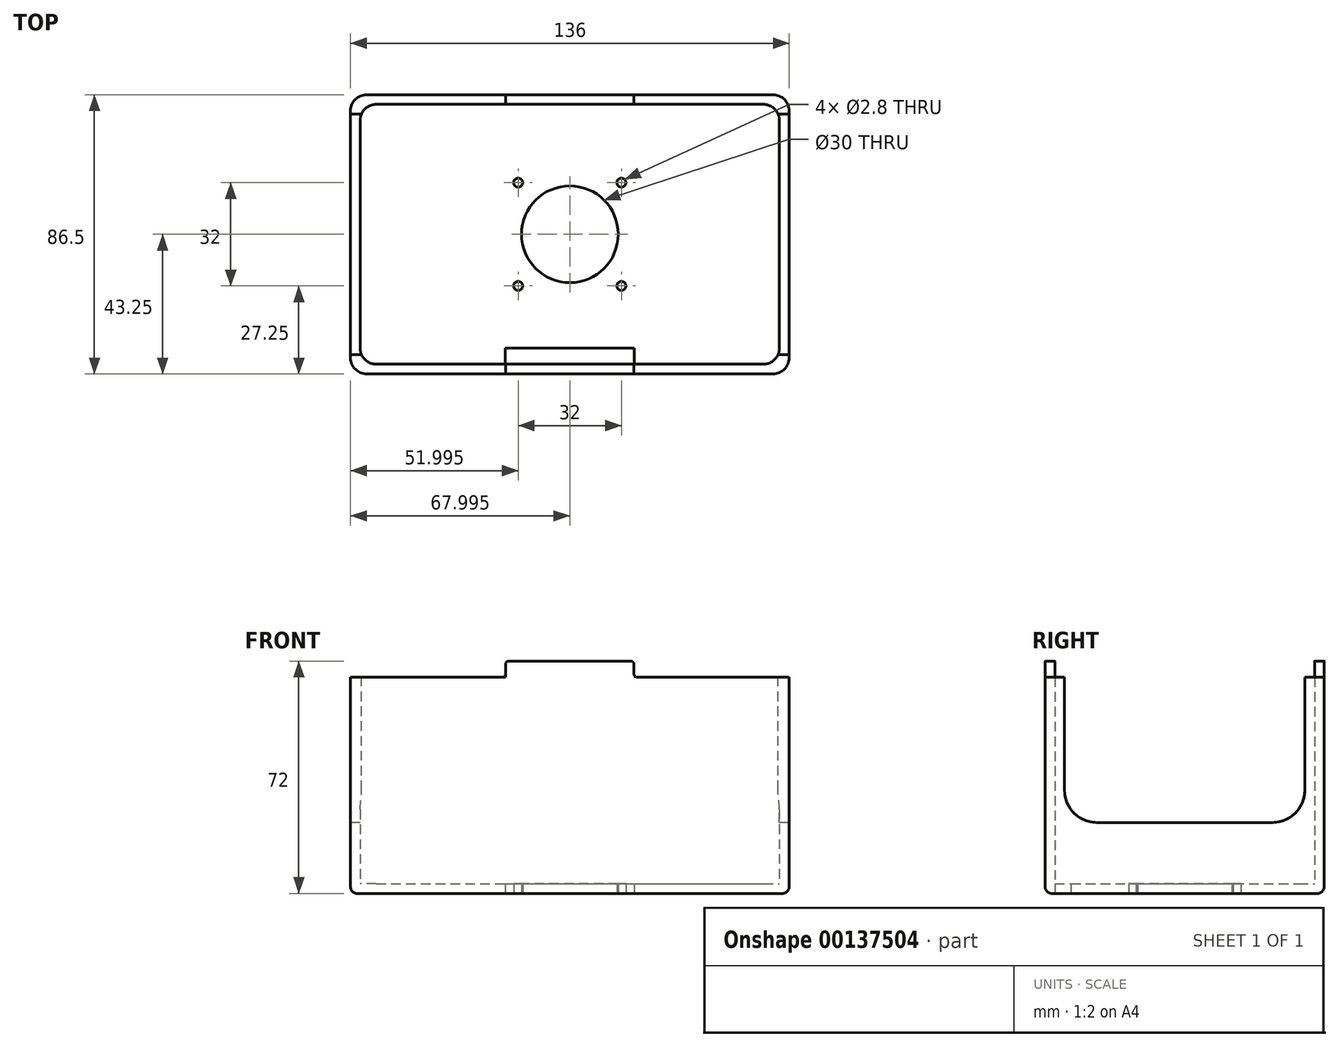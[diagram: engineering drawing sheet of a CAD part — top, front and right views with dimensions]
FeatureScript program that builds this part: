
annotation { "Feature Type Name" : "Feature", "Feature Type Description" : "" }
export const myFeature = defineFeature(function(context is Context, id is Id, definition is map)
    precondition{}
    {
        {
            var Q0;
            Q0=qCreatedBy(makeId("Top.planeOp"),FACE);
            var sketch = newSketch(context, id + "F0", { "sketchPlane" : qUnion([Q0])});
            skLineSegment(sketch, "E0.bottom", {"start": v(-60.37, 0) * mm, "end": v(69.63, 0) * mm});
            skLineSegment(sketch, "E0.top", {"start": v(-60.37, 92.5) * mm, "end": v(69.63, 92.5) * mm});
            skLineSegment(sketch, "E0.left", {"start": v(-60.37, 0) * mm, "end": v(-60.37, 92.5) * mm});
            skLineSegment(sketch, "E0.right", {"start": v(69.63, 0) * mm, "end": v(69.63, 92.5) * mm});
            skLineSegment(sketch, "E1.top", {"start": v(-60.37, 7) * mm, "end": v(69.63, 7) * mm});
            skLineSegment(sketch, "E1.left", {"start": v(-60.37, 0) * mm, "end": v(-60.37, 7) * mm});
            skLineSegment(sketch, "E1.right", {"start": v(69.63, 0) * mm, "end": v(69.63, 7) * mm});
            skLineSegment(sketch, "E2.bottom", {"start": v(-15.37, 7) * mm, "end": v(24.63, 7) * mm});
            skLineSegment(sketch, "E2.top", {"start": v(-15.37, 12) * mm, "end": v(24.63, 12) * mm});
            skLineSegment(sketch, "E2.left", {"start": v(-15.37, 7) * mm, "end": v(-15.37, 12) * mm});
            skLineSegment(sketch, "E2.right", {"start": v(24.63, 7) * mm, "end": v(24.63, 12) * mm});
            skPoint(sketch, "E3", {"position": v(4.63, 92.5) * mm});
            skPoint(sketch, "E4", {"position": v(4.63, 12) * mm});
            skLineSegment(sketch, "E5.top", {"start": v(-60.37, 87.5) * mm, "end": v(69.63, 87.5) * mm});
            skLineSegment(sketch, "E5.left", {"start": v(-60.37, 92.5) * mm, "end": v(-60.37, 87.5) * mm});
            skLineSegment(sketch, "E5.right", {"start": v(69.63, 92.5) * mm, "end": v(69.63, 87.5) * mm});
            skCircle(sketch, "E6", {"center": v(4.63, 47.25) * mm, "radius": 15 * mm});
            skCircle(sketch, "E7", {"center": v(20.63, 31.25) * mm, "radius": 1.4 * mm});
            skCircle(sketch, "E8", {"center": v(-11.37, 31.25) * mm, "radius": 1.4 * mm});
            skCircle(sketch, "E9", {"center": v(-11.37, 63.25) * mm, "radius": 1.4 * mm});
            skCircle(sketch, "E10", {"center": v(20.63, 63.25) * mm, "radius": 1.4 * mm});
            skLineSegment(sketch, "E11", {"start": v(20.63, 63.25) * mm, "end": v(20.63, 31.25) * mm, "construction": true});
            skLineSegment(sketch, "E12", {"start": v(-11.37, 63.25) * mm, "end": v(20.63, 63.25) * mm, "construction": true});
            skPoint(sketch, "E13", {"position": v(20.63, 47.25) * mm});
            skPoint(sketch, "E14", {"position": v(4.63, 63.25) * mm});
            skLineSegment(sketch, "E15", {"start": v(20.63, 63.25) * mm, "end": v(20.63, 87.5) * mm, "construction": true});
            skLineSegment(sketch, "E16", {"start": v(20.63, 31.25) * mm, "end": v(20.63, 7) * mm, "construction": true});
            skCircle(sketch, "E17", {"center": v(-30.37, 71.25) * mm, "radius": 3 * mm});
            skCircle(sketch, "E18", {"center": v(-30.37, 23.25) * mm, "radius": 3 * mm});
            skCircle(sketch, "E19", {"center": v(52.63, 71.25) * mm, "radius": 3 * mm});
            skCircle(sketch, "E20", {"center": v(52.63, 23.25) * mm, "radius": 3 * mm});
            skLineSegment(sketch, "E21", {"start": v(-30.37, 71.25) * mm, "end": v(52.63, 71.25) * mm, "construction": true});
            skLineSegment(sketch, "E22", {"start": v(52.63, 71.25) * mm, "end": v(52.63, 23.25) * mm, "construction": true});
            skCircle(sketch, "E23", {"center": v(-30.37, 71.25) * mm, "radius": 1.5 * mm});
            skCircle(sketch, "E24", {"center": v(-30.37, 23.25) * mm, "radius": 1.5 * mm});
            skCircle(sketch, "E25", {"center": v(52.63, 23.25) * mm, "radius": 1.5 * mm});
            skCircle(sketch, "E26", {"center": v(52.63, 71.25) * mm, "radius": 1.5 * mm});
            skLineSegment(sketch, "E27", {"start": v(52.63, 23.25) * mm, "end": v(52.63, 7) * mm, "construction": true});
            skLineSegment(sketch, "E28", {"start": v(52.63, 71.25) * mm, "end": v(52.63, 87.5) * mm, "construction": true});
            skLineSegment(sketch, "E29.bottom", {"start": v(-63.37, 4) * mm, "end": v(72.63, 4) * mm});
            skLineSegment(sketch, "E29.top", {"start": v(-63.37, 90.5) * mm, "end": v(72.63, 90.5) * mm});
            skLineSegment(sketch, "E29.left", {"start": v(-63.37, 4) * mm, "end": v(-63.37, 90.5) * mm});
            skLineSegment(sketch, "E29.right", {"start": v(72.63, 4) * mm, "end": v(72.63, 90.5) * mm});
            skLineSegment(sketch, "E30", {"start": v(4.63, 87.5) * mm, "end": v(4.63, 90.5) * mm});
            skPoint(sketch, "E30.startSnap0", {"position": v(4.63, 90.5) * mm});
            skLineSegment(sketch, "E31", {"start": v(-60.37, 27.6) * mm, "end": v(-63.37, 27.6) * mm});
            skLineSegment(sketch, "E32", {"start": v(14.88, 7) * mm, "end": v(14.88, 4) * mm});
            skLineSegment(sketch, "E33", {"start": v(69.63, 53.4) * mm, "end": v(72.63, 53.4) * mm});
            skLineSegment(sketch, "E34", {"start": v(-30.37, 71.25) * mm, "end": v(-60.37, 71.25) * mm});
            skSolve(sketch);
        }
        {
            var Q0;
            {var subQ2=sQuery(id+"F0.wireOp",EDGE,"E0.left");Q0=makeQuery(id+"F0.imprint","IMPRINT",FACE,{"disambiguationData":[TD([[makeQuery(id+"F0.imprint","IMPRINT",EDGE,{"derivedFrom":subQ2}),-1.0]])]});}
            var Q1;
            Q1=makeQuery(id+"F0.imprint","IMPRINT",FACE,{"disambiguationData":[TD([[makeQuery(id+"F0.imprint","IMPRINT",EDGE,{"derivedFrom":sQuery(id+"F0.wireOp",EDGE,"E2.bottom")}),1.0]])]});
            var Q2;
            Q2=makeQuery(id+"F0.imprint","IMPRINT",FACE,{"disambiguationData":[TD([[makeQuery(id+"F0.imprint","IMPRINT",EDGE,{"derivedFrom":sQuery(id+"F0.wireOp",EDGE,"E17")}),1.0]])]});
            var Q3;
            Q3=makeQuery(id+"F0.imprint","IMPRINT",FACE,{"disambiguationData":[TD([[makeQuery(id+"F0.imprint","IMPRINT",EDGE,{"derivedFrom":sQuery(id+"F0.wireOp",EDGE,"E23")}),1.0]])]});
            var Q4;
            Q4=makeQuery(id+"F0.imprint","IMPRINT",FACE,{"disambiguationData":[TD([[makeQuery(id+"F0.imprint","IMPRINT",EDGE,{"derivedFrom":sQuery(id+"F0.wireOp",EDGE,"E19")}),1.0]])]});
            var Q5;
            Q5=makeQuery(id+"F0.imprint","IMPRINT",FACE,{"disambiguationData":[TD([[makeQuery(id+"F0.imprint","IMPRINT",EDGE,{"derivedFrom":sQuery(id+"F0.wireOp",EDGE,"E26")}),1.0]])]});
            var Q6;
            Q6=makeQuery(id+"F0.imprint","IMPRINT",FACE,{"disambiguationData":[TD([[makeQuery(id+"F0.imprint","IMPRINT",EDGE,{"derivedFrom":sQuery(id+"F0.wireOp",EDGE,"E20")}),1.0]])]});
            var Q7;
            Q7=makeQuery(id+"F0.imprint","IMPRINT",FACE,{"disambiguationData":[TD([[makeQuery(id+"F0.imprint","IMPRINT",EDGE,{"derivedFrom":sQuery(id+"F0.wireOp",EDGE,"E25")}),1.0]])]});
            var Q8;
            Q8=makeQuery(id+"F0.imprint","IMPRINT",FACE,{"disambiguationData":[TD([[makeQuery(id+"F0.imprint","IMPRINT",EDGE,{"derivedFrom":sQuery(id+"F0.wireOp",EDGE,"E18")}),1.0]])]});
            var Q9;
            Q9=makeQuery(id+"F0.imprint","IMPRINT",FACE,{"disambiguationData":[TD([[makeQuery(id+"F0.imprint","IMPRINT",EDGE,{"derivedFrom":sQuery(id+"F0.wireOp",EDGE,"E24")}),1.0]])]});
            extrude(context, id + "F1", {"entities" : qUnion([Q0, Q1, Q2, Q3, Q4, Q5, Q6, Q7, Q8, Q9]), "depth" : 3 * mm});
        }
        {
            var Q0;
            {var subQ3=sQuery(id+"F0.wireOp",EDGE,"E31");Q0=makeQuery(id+"F0.imprint","IMPRINT",FACE,{"disambiguationData":[TD([[makeQuery(id+"F0.imprint","IMPRINT",EDGE,{"derivedFrom":subQ3}),-1.0]])]});}
            var Q1;
            {var subQ3=sQuery(id+"F0.wireOp",EDGE,"E30");Q1=makeQuery(id+"F0.imprint","IMPRINT",FACE,{"disambiguationData":[TD([[makeQuery(id+"F0.imprint","IMPRINT",EDGE,{"derivedFrom":subQ3}),1.0]])]});}
            var Q2;
            {var subQ3=sQuery(id+"F0.wireOp",EDGE,"E30");Q2=makeQuery(id+"F0.imprint","IMPRINT",FACE,{"disambiguationData":[TD([[makeQuery(id+"F0.imprint","IMPRINT",EDGE,{"derivedFrom":subQ3}),-1.0]])]});}
            var Q3;
            {var subQ3=sQuery(id+"F0.wireOp",EDGE,"E33");Q3=makeQuery(id+"F0.imprint","IMPRINT",FACE,{"disambiguationData":[TD([[makeQuery(id+"F0.imprint","IMPRINT",EDGE,{"derivedFrom":subQ3}),1.0]])]});}
            var Q4;
            {var subQ3=sQuery(id+"F0.wireOp",EDGE,"E33");Q4=makeQuery(id+"F0.imprint","IMPRINT",FACE,{"disambiguationData":[TD([[makeQuery(id+"F0.imprint","IMPRINT",EDGE,{"derivedFrom":subQ3}),-1.0]])]});}
            var Q5;
            {var subQ0=sQuery(id+"F0.wireOp",EDGE,"E32");Q5=makeQuery(id+"F0.imprint","IMPRINT",FACE,{"disambiguationData":[TD([[makeQuery(id+"F0.imprint","IMPRINT",EDGE,{"derivedFrom":subQ0}),1.0]])]});}
            var Q6;
            {var subQ3=sQuery(id+"F0.wireOp",EDGE,"E32");Q6=makeQuery(id+"F0.imprint","IMPRINT",FACE,{"disambiguationData":[TD([[makeQuery(id+"F0.imprint","IMPRINT",EDGE,{"derivedFrom":subQ3}),-1.0]])]});}
            var Q7;
            {var subQ3=sQuery(id+"F0.wireOp",EDGE,"E31");Q7=makeQuery(id+"F0.imprint","IMPRINT",FACE,{"disambiguationData":[TD([[makeQuery(id+"F0.imprint","IMPRINT",EDGE,{"derivedFrom":subQ3}),1.0]])]});}
            extrude(context, id + "F2", {"entities" : qUnion([Q0, Q1, Q2, Q3, Q4, Q5, Q6, Q7]), "operationType" : NewBodyOperationType.ADD, "depth" : 67 * mm});
        }
        {
            var Q0;
            Q0=makeQuery(id+"F2.opExtrude","SWEPT_FACE",FACE,{"disambiguationData":[OSD([sQuery(id+"F0.wireOp",EDGE,"E29.left")])]});
            var sketch = newSketch(context, id + "F3", { "sketchPlane" : qUnion([Q0])});
            skCircle(sketch, "E35", {"center": v(-20, 31.97) * mm, "radius": 10 * mm});
            skPoint(sketch, "E36", {"position": v(-57.96, 0) * mm});
            skLineSegment(sketch, "E37", {"start": v(-30, 31.97) * mm, "end": v(-30, 67) * mm});
            skLineSegment(sketch, "E38", {"start": v(-10, 31.97) * mm, "end": v(-10, 67) * mm});
            skCircle(sketch, "E39", {"center": v(-74.5, 31.97) * mm, "radius": 10 * mm});
            skLineSegment(sketch, "E40", {"start": v(-84.5, 31.97) * mm, "end": v(-84.5, 67) * mm});
            skLineSegment(sketch, "E41", {"start": v(-64.5, 31.97) * mm, "end": v(-64.5, 46.86) * mm});
            skLineSegment(sketch, "E42", {"start": v(-20, 21.97) * mm, "end": v(-74.5, 21.97) * mm});
            skLineSegment(sketch, "E43", {"start": v(-64.5, 31.97) * mm, "end": v(-30, 31.97) * mm});
            skPoint(sketch, "E44", {"position": v(-47.25, 31.97) * mm});
            skPoint(sketch, "E45", {"position": v(-47.25, 67) * mm});
            skSolve(sketch);
        }
        {
            var Q0;
            Q0=makeQuery(id+"F3.imprint","IMPRINT",FACE,{"disambiguationData":[TD([[makeQuery(id+"F3.imprint","IMPRINT",EDGE,{"derivedFrom":sQuery(id+"F3.wireOp",EDGE,"Rx419f1T-JsYL-VPEE-dF0Y-VFoqTHM8m6fg.bottom")}),1.0]])]});
            var Q1;
            Q1=makeQuery(id+"F3.imprint","IMPRINT",FACE,{"disambiguationData":[TD([[makeQuery(id+"F3.imprint","IMPRINT",EDGE,{"derivedFrom":sQuery(id+"F3.wireOp",EDGE,"E35")}),1.0]])]});
            var Q2;
            {var subQ0=sQuery(id+"F3.wireOp",EDGE,"E37");Q2=makeQuery(id+"F3.imprint","IMPRINT",FACE,{"disambiguationData":[TD([[makeQuery(id+"F3.imprint","IMPRINT",EDGE,{"derivedFrom":subQ0}),-1.0]])]});}
            var Q3;
            {var subQ0=sQuery(id+"F3.wireOp",EDGE,"E39");var subQ1=makeQuery(id+"F3.imprint","INTERSECT",VERTEX,{"derivedFrom":[subQ0,sQuery(id+"F3.wireOp",EDGE,"E40")]});Q3=makeQuery(id+"F3.imprint","IMPRINT",FACE,{"disambiguationData":[TD([[makeQuery(id+"F3.imprint","IMPRINT",EDGE,{"disambiguationData":[TD([[subQ1,-1.0]])],"derivedFrom":subQ0}),1.0]])]});}
            var Q4;
            {var subQ0=sQuery(id+"F3.wireOp",EDGE,"E40");Q4=makeQuery(id+"F3.imprint","IMPRINT",FACE,{"disambiguationData":[TD([[makeQuery(id+"F3.imprint","IMPRINT",EDGE,{"derivedFrom":subQ0}),-1.0]])]});}
            var Q5;
            {var subQ0=sQuery(id+"F3.wireOp",EDGE,"E37");Q5=makeQuery(id+"F3.imprint","IMPRINT",FACE,{"disambiguationData":[TD([[makeQuery(id+"F3.imprint","IMPRINT",EDGE,{"derivedFrom":subQ0}),1.0]])]});}
            var Q6;
            {var subQ2=sQuery(id+"F3.wireOp",EDGE,"E42");Q6=makeQuery(id+"F3.imprint","IMPRINT",FACE,{"disambiguationData":[TD([[makeQuery(id+"F3.imprint","IMPRINT",EDGE,{"derivedFrom":subQ2}),-1.0]])]});}
            extrude(context, id + "F4", {"entities" : qUnion([Q0, Q1, Q2, Q3, Q4, Q5, Q6]), "operationType" : NewBodyOperationType.REMOVE, "endBound" : BoundingType.THROUGH_ALL, "oppositeDirection" : true, "depth" : 25 * mm});
        }
        {
            var Q0;
            Q0=makeQuery(id+"F2.opExtrude","CAP_FACE",FACE,{"disambiguationData":[OSD([sQuery(id+"F0.wireOp",EDGE,"E0.left"),sQuery(id+"F0.wireOp",EDGE,"E0.right"),sQuery(id+"F0.wireOp",EDGE,"E1.top"),sQuery(id+"F0.wireOp",EDGE,"E2.bottom"),sQuery(id+"F0.wireOp",EDGE,"E5.top"),sQuery(id+"F0.wireOp",EDGE,"E29.bottom"),sQuery(id+"F0.wireOp",EDGE,"E29.top"),sQuery(id+"F0.wireOp",EDGE,"E29.left"),sQuery(id+"F0.wireOp",EDGE,"E29.right")])],"isStart":false});
            var sketch = newSketch(context, id + "F5", { "sketchPlane" : qUnion([Q0])});
            skLineSegment(sketch, "E46.bottom", {"start": v(-15.27, 7) * mm, "end": v(24.53, 7) * mm});
            skLineSegment(sketch, "E46.top", {"start": v(-15.27, 4) * mm, "end": v(24.53, 4) * mm});
            skLineSegment(sketch, "E46.left", {"start": v(-15.27, 7) * mm, "end": v(-15.27, 4) * mm});
            skLineSegment(sketch, "E46.right", {"start": v(24.53, 7) * mm, "end": v(24.53, 4) * mm});
            skPoint(sketch, "E47", {"position": v(4.63, 87.5) * mm});
            skPoint(sketch, "E48", {"position": v(4.63, 7) * mm});
            skSolve(sketch);
        }
        {
            var Q0;
            {var subQ0=sQuery(id+"F0.wireOp",EDGE,"E29.top");var subQ1=sQuery(id+"F0.wireOp",EDGE,"E5.top");var subQ2=sQuery(id+"F0.wireOp",EDGE,"E0.right");var subQ3=sQuery(id+"F0.wireOp",EDGE,"E0.left");var subQ4=sQuery(id+"F0.wireOp",EDGE,"E29.left");var subQ5=sQuery(id+"F0.wireOp",EDGE,"E29.right");Q0=makeQuery(id+"F4.boolean.opBoolean","SPLIT",FACE,{"disambiguationData":[TD([makeQuery(id+"F2.opExtrude","SWEPT_FACE",FACE,{"disambiguationData":[OSD([subQ1])]})])],"derivedFrom":makeQuery(id+"F2.opExtrude","CAP_FACE",FACE,{"disambiguationData":[OSD([subQ3,subQ2,sQuery(id+"F0.wireOp",EDGE,"E1.top"),sQuery(id+"F0.wireOp",EDGE,"E2.bottom"),subQ1,sQuery(id+"F0.wireOp",EDGE,"E29.bottom"),subQ0,subQ4,subQ5])],"isStart":false})});}
            var sketch = newSketch(context, id + "F6", { "sketchPlane" : qUnion([Q0])});
            skPoint(sketch, "E49", {"position": v(4.63, 87.5) * mm});
            skLineSegment(sketch, "E50.bottom", {"start": v(24.53, 87.5) * mm, "end": v(-15.27, 87.5) * mm});
            skLineSegment(sketch, "E50.top", {"start": v(24.53, 90.5) * mm, "end": v(-15.27, 90.5) * mm});
            skLineSegment(sketch, "E50.left", {"start": v(24.53, 87.5) * mm, "end": v(24.53, 90.5) * mm});
            skLineSegment(sketch, "E50.right", {"start": v(-15.27, 87.5) * mm, "end": v(-15.27, 90.5) * mm});
            skPoint(sketch, "E51", {"position": v(4.63, 90.5) * mm});
            skSolve(sketch);
        }
        {
            var Q0;
            Q0=qSketchRegion(id+"F5",true);
            var Q1;
            Q1=makeQuery(id+"F6.imprint","IMPRINT",FACE,{"disambiguationData":[TD([[makeQuery(id+"F6.imprint","IMPRINT",EDGE,{"derivedFrom":sQuery(id+"F6.wireOp",EDGE,"E50.bottom")}),1.0]])]});
            extrude(context, id + "F7", {"entities" : qUnion([Q0, Q1]), "operationType" : NewBodyOperationType.ADD, "depth" : 5 * mm});
        }
        {
            var Q0;
            Q0=makeQuery(id+"F7.opExtrude","CAP_EDGE",EDGE,{"disambiguationData":[OSD([sQuery(id+"F5.wireOp",EDGE,"E46.left")])],"isStart":true});
            var Q1;
            Q1=makeQuery(id+"F7.opExtrude","CAP_EDGE",EDGE,{"disambiguationData":[OSD([sQuery(id+"F5.wireOp",EDGE,"E46.left")])],"isStart":false});
            var Q2;
            Q2=makeQuery(id+"F7.opExtrude","CAP_EDGE",EDGE,{"disambiguationData":[OSD([sQuery(id+"F5.wireOp",EDGE,"E46.right")])],"isStart":false});
            var Q3;
            Q3=makeQuery(id+"F7.opExtrude","CAP_EDGE",EDGE,{"disambiguationData":[OSD([sQuery(id+"F5.wireOp",EDGE,"E46.right")])],"isStart":true});
            var Q4;
            Q4=makeQuery(id+"F7.opExtrude","CAP_EDGE",EDGE,{"disambiguationData":[OSD([sQuery(id+"F6.wireOp",EDGE,"E50.right")])],"isStart":true});
            var Q5;
            Q5=makeQuery(id+"F7.opExtrude","CAP_EDGE",EDGE,{"disambiguationData":[OSD([sQuery(id+"F6.wireOp",EDGE,"E50.right")])],"isStart":false});
            var Q6;
            Q6=makeQuery(id+"F7.opExtrude","CAP_EDGE",EDGE,{"disambiguationData":[OSD([sQuery(id+"F6.wireOp",EDGE,"E50.left")])],"isStart":false});
            var Q7;
            Q7=makeQuery(id+"F7.opExtrude","CAP_EDGE",EDGE,{"disambiguationData":[OSD([sQuery(id+"F6.wireOp",EDGE,"E50.left")])],"isStart":true});
            fillet(context, id + "F8", {"entities" : qUnion([Q0, Q1, Q2, Q3, Q4, Q5, Q6, Q7]), "radius" : 1 * mm, "tangentPropagation" : true, "allowEdgeOverflow" : false});
        }
        {
            var Q0;
            Q0=makeQuery(id+"F2.opExtrude","SWEPT_EDGE",EDGE,{"disambiguationData":[OSD([sQuery(id+"F0.wireOp",EDGE,"E29.bottom"),sQuery(id+"F0.wireOp",EDGE,"E29.right")])]});
            var Q1;
            Q1=makeQuery(id+"F2.opExtrude","SWEPT_EDGE",EDGE,{"disambiguationData":[OSD([sQuery(id+"F0.wireOp",EDGE,"E29.top"),sQuery(id+"F0.wireOp",EDGE,"E29.right")])]});
            var Q2;
            Q2=makeQuery(id+"F2.opExtrude","SWEPT_EDGE",EDGE,{"disambiguationData":[OSD([sQuery(id+"F0.wireOp",EDGE,"E29.top"),sQuery(id+"F0.wireOp",EDGE,"E29.left")])]});
            var Q3;
            Q3=makeQuery(id+"F2.opExtrude","SWEPT_EDGE",EDGE,{"disambiguationData":[OSD([sQuery(id+"F0.wireOp",EDGE,"E29.bottom"),sQuery(id+"F0.wireOp",EDGE,"E29.left")])]});
            var Q4;
            Q4=makeQuery(id+"F2.opExtrude","SWEPT_EDGE",EDGE,{"disambiguationData":[OSD([sQuery(id+"F0.wireOp",EDGE,"E0.left"),sQuery(id+"F0.wireOp",EDGE,"E1.top"),sQuery(id+"F0.wireOp",EDGE,"E1.left")])]});
            var Q5;
            Q5=makeQuery(id+"F2.opExtrude","SWEPT_EDGE",EDGE,{"disambiguationData":[OSD([sQuery(id+"F0.wireOp",EDGE,"E0.left"),sQuery(id+"F0.wireOp",EDGE,"E5.top"),sQuery(id+"F0.wireOp",EDGE,"E5.left")])]});
            var Q6;
            Q6=makeQuery(id+"F2.opExtrude","SWEPT_EDGE",EDGE,{"disambiguationData":[OSD([sQuery(id+"F0.wireOp",EDGE,"E0.right"),sQuery(id+"F0.wireOp",EDGE,"E5.top"),sQuery(id+"F0.wireOp",EDGE,"E5.right")])]});
            var Q7;
            Q7=makeQuery(id+"F2.opExtrude","SWEPT_EDGE",EDGE,{"disambiguationData":[OSD([sQuery(id+"F0.wireOp",EDGE,"E0.right"),sQuery(id+"F0.wireOp",EDGE,"E1.top"),sQuery(id+"F0.wireOp",EDGE,"E1.right")])]});
            fillet(context, id + "F9", {"entities" : qUnion([Q0, Q1, Q2, Q3, Q4, Q5, Q6, Q7]), "radius" : 5 * mm, "tangentPropagation" : true, "allowEdgeOverflow" : false});
        }
        {
            var Q0;
            Q0=makeQuery(id+"F1.opExtrude","CAP_EDGE",EDGE,{"disambiguationData":[OSD([sQuery(id+"F0.wireOp",EDGE,"E5.top")])],"isStart":false});
            var Q1;
            Q1=makeQuery(id+"F2.opExtrude","CAP_EDGE",EDGE,{"disambiguationData":[OSD([sQuery(id+"F0.wireOp",EDGE,"E29.bottom")])],"isStart":true});
            fillet(context, id + "F10", {"entities" : qUnion([Q0, Q1]), "radius" : 2 * mm, "tangentPropagation" : true, "allowEdgeOverflow" : false});
        }
    });
